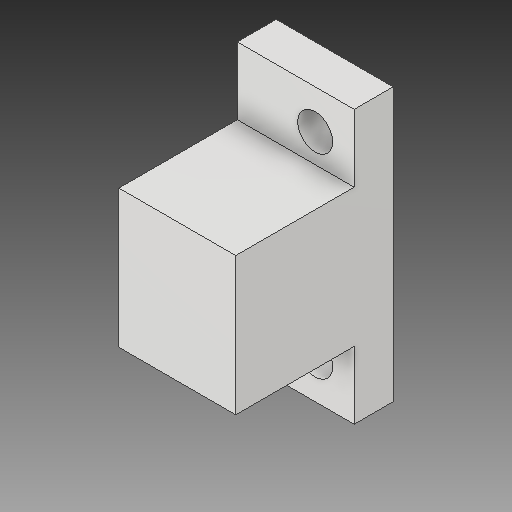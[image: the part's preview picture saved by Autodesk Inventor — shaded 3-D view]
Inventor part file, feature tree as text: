
AUTODESK INVENTOR PART (.ipt)
format: ipt  version: 2019.3 (Build 233278000, 278)  size: 136,192 bytes
history: native  units: mm
features: reference x4, extrude x3, sketch x3, other x3
ambient origin geometry x8: Origin, YZ Plane, XZ Plane, XY Plane, X Axis, Y Axis, Z Axis, Center Point
bodies: Solid1 (feature_tree)
feature tree (13):
  extrude  "Extrusion1"  Depth=30.0mm
  extrude  "Extrusion2"  Depth=5.0mm
  extrude  "Extrusion3"  Depth=35.4mm TaperAngle=0.0deg
  sketch  "Sketch1"  dims[d1=30.0mm d2=60.0mm]
  reference  "Reference1"
  reference  "Reference2"
  reference  "Reference3"
  reference  "Reference4"
  sketch  "Sketch2"  dims[d5=10.0mm d6=0.0mm d7=5.0mm]
  sketch  "Sketch3"  dims[d8=30.4mm d9=0.0mm d18=35.4mm d19=0.0mm d21=25.4mm d22=25.4mm d23=5.0mm d24=5.0mm d26=35.4mm d27=17.3mm d28=10.0mm d29=10.0mm]
  parser-record x1  (decoder bookkeeping rows leaked as tree rows — omitted from the tree; the rows remain in map.json)
  other  "Assembly.iam"
  other  "CameraBracket:1"
note: 1 file-system path scrubbed to <path> (originals preserved in map.json)
